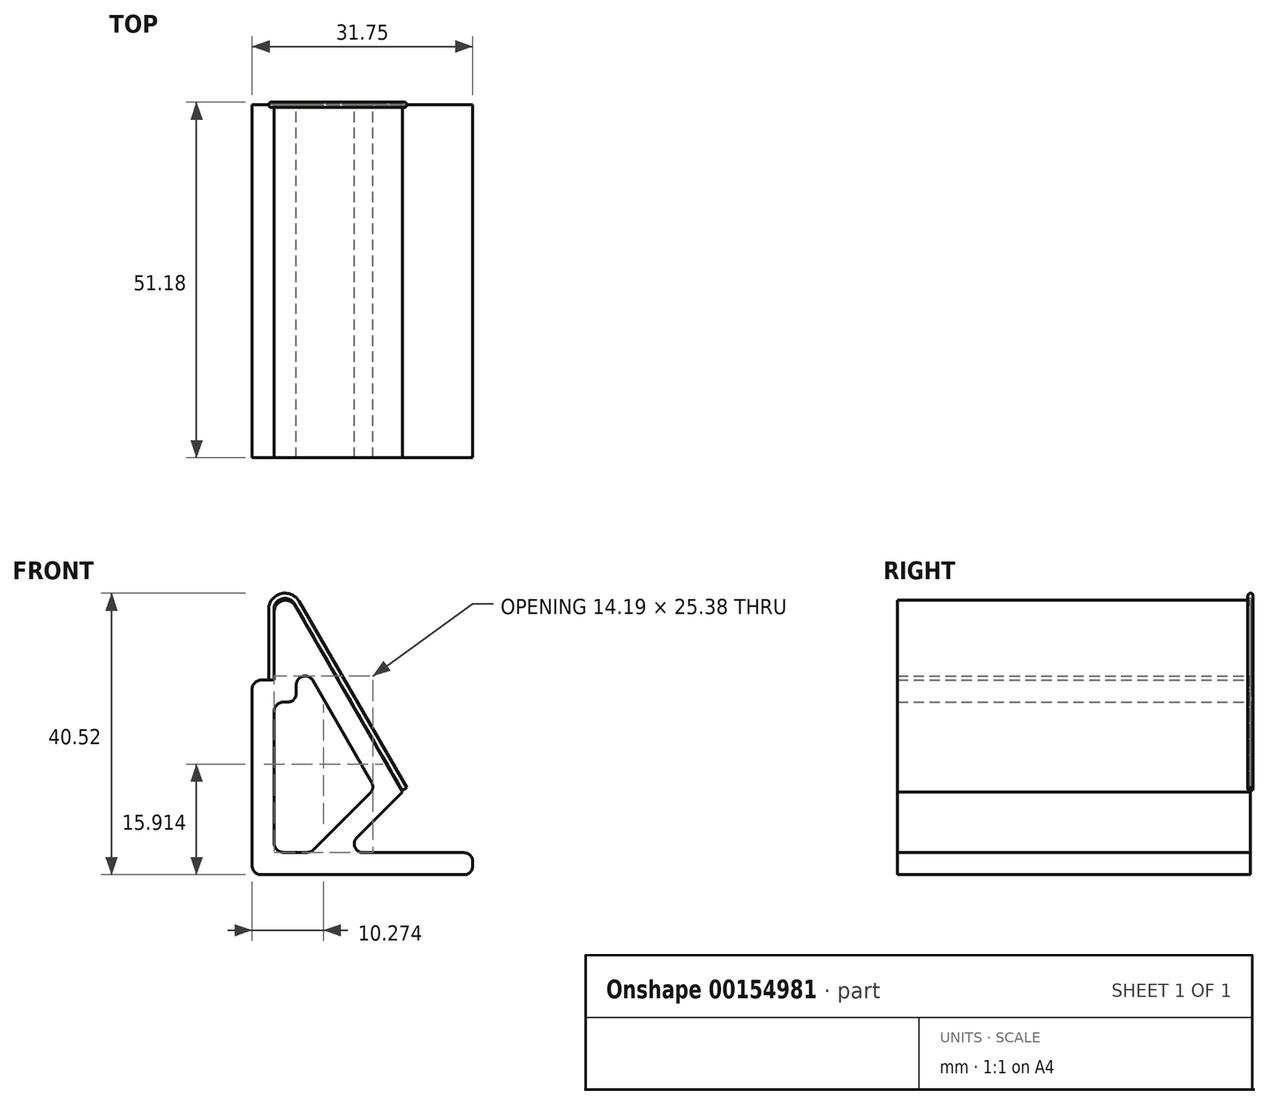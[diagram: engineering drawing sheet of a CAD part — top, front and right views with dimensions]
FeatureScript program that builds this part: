
annotation { "Feature Type Name" : "Feature", "Feature Type Description" : "" }
export const myFeature = defineFeature(function(context is Context, id is Id, definition is map)
    precondition{}
    {
        {
            var Q0;
            Q0=qCreatedBy(makeId("Front.planeOp"),FACE);
            var sketch = newSketch(context, id + "F0", { "sketchPlane" : qUnion([Q0])});
            skLineSegment(sketch, "E0", {"start": v(0, 0) * mm, "end": v(0, 10.16) * mm});
            skLineSegment(sketch, "E1", {"start": v(3.68, 11.15) * mm, "end": v(19.17, -15.7) * mm});
            skArc(sketch, "E2", {"start": v(3.68, 11.15) * mm, "mid": v(1.46, 12.06) * mm, "end": v(0, 10.16) * mm});
            skSolve(sketch);
        }
        {
            var Q0;
            Q0=qCreatedBy(makeId("Top.planeOp"),FACE);
            var sketch = newSketch(context, id + "F1", { "sketchPlane" : qUnion([Q0])});
            skCircle(sketch, "E3", {"center": v(0, 0) * mm, "radius": 0.38 * mm});
            skSolve(sketch);
        }
        {
            var Q0;
            Q0 = qSketchRegion(id + "F1", true);
            var Q1;
            Q1 = qConstructionFilter(qBodyType(qCreatedBy(id + "F0" ,EDGE), BodyType.WIRE), ConstructionObject.NO);
            sweep(context, id + "F2", {"profiles" : qUnion([Q0]), "path" : qUnion([Q1])});
        }
        {
            var Q0;
            Q0=qCreatedBy(makeId("Front.planeOp"),FACE);
            var sketch = newSketch(context, id + "F3", { "sketchPlane" : qUnion([Q0])});
            skLineSegment(sketch, "E4", {"start": v(27.73, -28.01) * mm, "end": v(-1.48, -28.01) * mm});
            skLineSegment(sketch, "E5", {"start": v(-2.75, -26.74) * mm, "end": v(-2.75, -1.27) * mm});
            skLineSegment(sketch, "E6", {"start": v(29, -26.1) * mm, "end": v(29, -26.74) * mm});
            skArc(sketch, "E7", {"start": v(3.45, 10.68) * mm, "mid": v(1.63, 11.43) * mm, "end": v(0.43, 9.87) * mm});
            skLineSegment(sketch, "E8", {"start": v(3.45, 10.68) * mm, "end": v(18.9, -16.08) * mm});
            skLineSegment(sketch, "E9", {"start": v(18.9, -16.08) * mm, "end": v(12.32, -22.67) * mm});
            skLineSegment(sketch, "E10", {"start": v(13.22, -24.84) * mm, "end": v(27.73, -24.84) * mm});
            skLineSegment(sketch, "E11", {"start": v(0.43, 9.87) * mm, "end": v(0.43, 0) * mm});
            skLineSegment(sketch, "E12", {"start": v(0.43, 0) * mm, "end": v(-1.48, 0) * mm});
            skLineSegment(sketch, "E13", {"start": v(1.7, -24.78) * mm, "end": v(5.19, -24.78) * mm});
            skLineSegment(sketch, "E14", {"start": v(6.09, -24.41) * mm, "end": v(14.25, -16.25) * mm});
            skLineSegment(sketch, "E15", {"start": v(14.45, -14.72) * mm, "end": v(5.97, -0.04) * mm});
            skLineSegment(sketch, "E16", {"start": v(3.6, -0.68) * mm, "end": v(3.6, -1.9) * mm});
            skLineSegment(sketch, "E17", {"start": v(2.33, -3.18) * mm, "end": v(1.7, -3.18) * mm});
            skLineSegment(sketch, "E18", {"start": v(0.43, -4.45) * mm, "end": v(0.43, -23.51) * mm});
            skPoint(sketch, "E19.visualSharp", {"position": v(-2.75, -28.01) * mm});
            skArc(sketch, "E19.filletArc", {"start": v(-2.75, -26.74) * mm, "mid": v(-2.37, -27.64) * mm, "end": v(-1.48, -28.01) * mm});
            skPoint(sketch, "E20.visualSharp", {"position": v(0.43, -24.78) * mm});
            skArc(sketch, "E20.filletArc", {"start": v(0.43, -23.51) * mm, "mid": v(0.8, -24.41) * mm, "end": v(1.7, -24.78) * mm});
            skPoint(sketch, "E21.visualSharp", {"position": v(5.71, -24.78) * mm});
            skArc(sketch, "E21.filletArc", {"start": v(5.19, -24.78) * mm, "mid": v(5.67, -24.69) * mm, "end": v(6.09, -24.41) * mm});
            skPoint(sketch, "E22.visualSharp", {"position": v(10.15, -24.84) * mm});
            skArc(sketch, "E22.filletArc", {"start": v(12.32, -22.67) * mm, "mid": v(12.04, -24.05) * mm, "end": v(13.22, -24.84) * mm});
            skPoint(sketch, "E23.visualSharp", {"position": v(14.94, -15.56) * mm});
            skArc(sketch, "E23.filletArc", {"start": v(14.25, -16.25) * mm, "mid": v(14.6, -15.52) * mm, "end": v(14.45, -14.72) * mm});
            skPoint(sketch, "E24.visualSharp", {"position": v(29, -24.84) * mm});
            skArc(sketch, "E24.filletArc", {"start": v(29, -26.1) * mm, "mid": v(28.63, -25.21) * mm, "end": v(27.73, -24.84) * mm});
            skPoint(sketch, "E25.visualSharp", {"position": v(29, -28.01) * mm});
            skArc(sketch, "E25.filletArc", {"start": v(27.73, -28.01) * mm, "mid": v(28.63, -27.64) * mm, "end": v(29, -26.74) * mm});
            skPoint(sketch, "E26.visualSharp", {"position": v(0.43, -3.18) * mm});
            skArc(sketch, "E26.filletArc", {"start": v(1.7, -3.18) * mm, "mid": v(0.8, -3.55) * mm, "end": v(0.43, -4.45) * mm});
            skPoint(sketch, "E27.visualSharp", {"position": v(3.6, -3.17) * mm});
            skArc(sketch, "E27.filletArc", {"start": v(2.33, -3.17) * mm, "mid": v(3.23, -2.8) * mm, "end": v(3.6, -1.9) * mm});
            skPoint(sketch, "E28.visualSharp", {"position": v(3.6, 4.06) * mm});
            skArc(sketch, "E28.filletArc", {"start": v(5.97, -0.04) * mm, "mid": v(4.55, 0.55) * mm, "end": v(3.6, -0.68) * mm});
            skPoint(sketch, "E29.visualSharp", {"position": v(-2.75, 0) * mm});
            skArc(sketch, "E29.filletArc", {"start": v(-1.48, 0) * mm, "mid": v(-2.37, -0.37) * mm, "end": v(-2.75, -1.27) * mm});
            skSolve(sketch);
        }
        {
            var Q0;
            Q0 = qSketchRegion(id + "F3", true);
            extrude(context, id + "F4", {"entities" : qUnion([Q0]), "depth" : 50.8 * mm});
        }
    });
